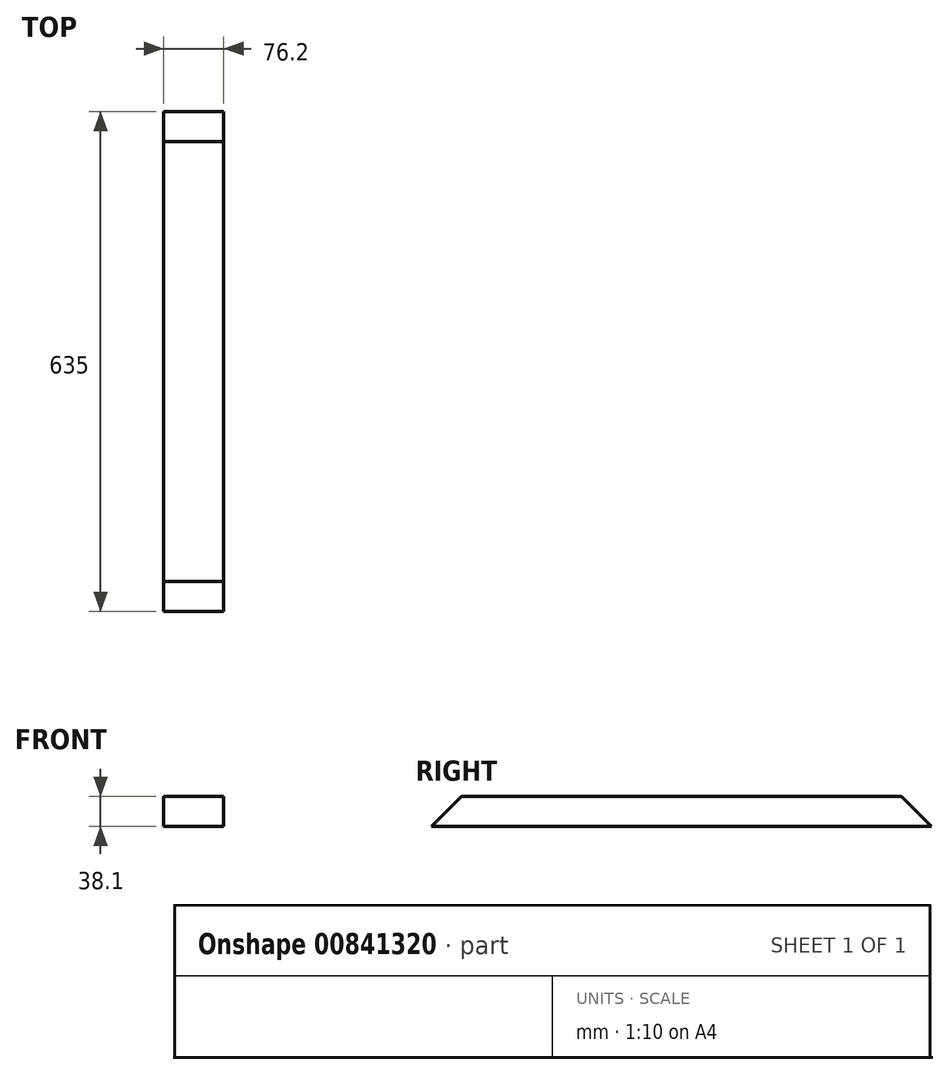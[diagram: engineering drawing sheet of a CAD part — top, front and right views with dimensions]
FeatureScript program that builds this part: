
annotation { "Feature Type Name" : "Feature", "Feature Type Description" : "" }
export const myFeature = defineFeature(function(context is Context, id is Id, definition is map)
    precondition{}
    {
        {
            var Q0;
            Q0=qCreatedBy(makeId("Front.planeOp"),FACE);
            var sketch = newSketch(context, id + "F0", { "sketchPlane" : qUnion([Q0])});
            skLineSegment(sketch, "E0.bottom", {"start": v(-38.1, 19.05) * mm, "end": v(38.1, 19.05) * mm});
            skLineSegment(sketch, "E0.top", {"start": v(-38.1, -19.05) * mm, "end": v(38.1, -19.05) * mm});
            skLineSegment(sketch, "E0.left", {"start": v(-38.1, 19.05) * mm, "end": v(-38.1, -19.05) * mm});
            skLineSegment(sketch, "E0.right", {"start": v(38.1, 19.05) * mm, "end": v(38.1, -19.05) * mm});
            skSolve(sketch);
        }
        {
            var Q0;
            Q0 = qSketchRegion(id + "F0", true);
            extrude(context, id + "F1", {"entities" : qUnion([Q0]), "depth" : 317.5 * mm, "offsetDistance" : 25.4 * mm, "hasSecondDirection" : true, "secondDirectionOppositeDirection" : true, "secondDirectionDepth" : 317.5 * mm});
        }
        {
            var Q0;
            Q0=makeQuery(id+"F1.opExtrude","SWEPT_FACE",FACE,{"disambiguationData":[OSD([sQuery(id+"F0.wireOp",EDGE,"E0.left")])]});
            var sketch = newSketch(context, id + "F2", { "sketchPlane" : qUnion([Q0])});
            skLineSegment(sketch, "E1", {"start": v(-317.5, 19.05) * mm, "end": v(-317.5, -19.05) * mm});
            skLineSegment(sketch, "E2", {"start": v(-317.5, -19.05) * mm, "end": v(-279.4, 19.05) * mm});
            skLineSegment(sketch, "E3", {"start": v(-279.4, 19.05) * mm, "end": v(-317.5, 19.05) * mm});
            skLineSegment(sketch, "E4", {"start": v(317.5, -19.05) * mm, "end": v(317.5, 19.05) * mm});
            skLineSegment(sketch, "E5", {"start": v(317.5, 19.05) * mm, "end": v(279.4, 19.05) * mm});
            skLineSegment(sketch, "E6", {"start": v(279.4, 19.05) * mm, "end": v(317.5, -19.05) * mm});
            skSolve(sketch);
        }
        {
            var Q0;
            Q0 = qSketchRegion(id + "F2", true);
            extrude(context, id + "F3", {"entities" : qUnion([Q0]), "operationType" : NewBodyOperationType.REMOVE, "endBound" : BoundingType.UP_TO_NEXT, "oppositeDirection" : true, "depth" : 25.4 * mm, "offsetDistance" : 25.4 * mm});
        }
    });
